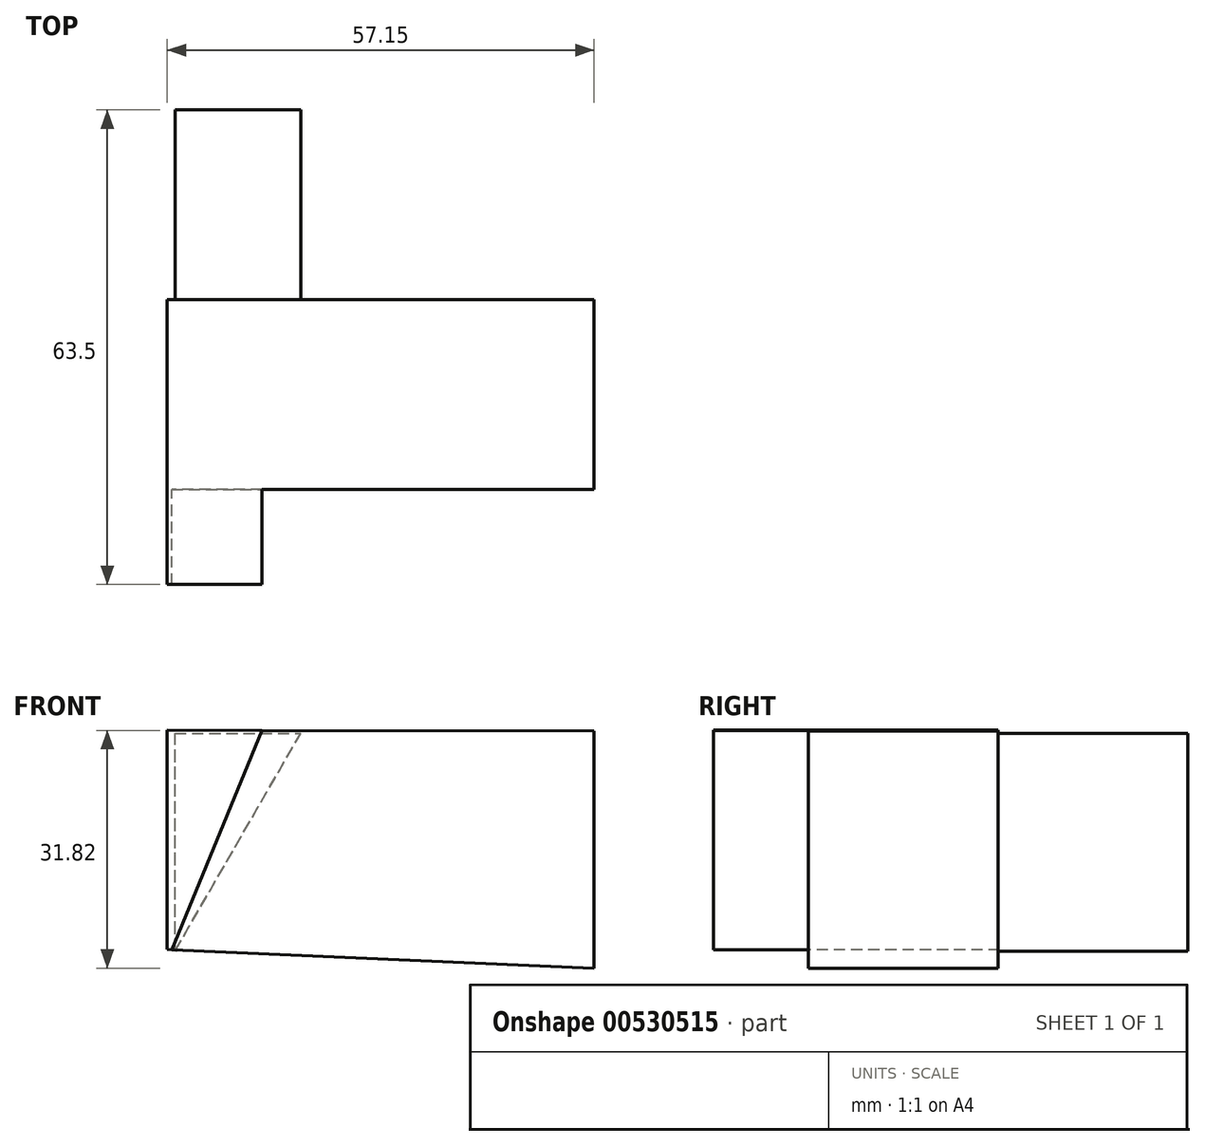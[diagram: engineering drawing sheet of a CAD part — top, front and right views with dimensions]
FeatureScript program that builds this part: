
annotation { "Feature Type Name" : "Feature", "Feature Type Description" : "" }
export const myFeature = defineFeature(function(context is Context, id is Id, definition is map)
    precondition{}
    {
        {
            var Q0;
            Q0=makeQuery(id+"FD3Ji2dYKjyLdMA_0.opExtrude","CAP_FACE",FACE,{"disambiguationData":[OSD([sQuery(id+"FqsT9jO7adyWTyq_0.wireOp",EDGE,"Xv4BoJzN-Ed49-FRgB-tAfS-qI5ulcrlhC3v"),sQuery(id+"FqsT9jO7adyWTyq_0.wireOp",EDGE,"Rq2qgrAZ-CMcJ-hNfP-7aXm-7j5Vf8qbodJT"),sQuery(id+"FqsT9jO7adyWTyq_0.wireOp",EDGE,"Tq6V1iMk-VQIz-2OuW-ugdr-rw9odok06HOZ"),sQuery(id+"FqsT9jO7adyWTyq_0.wireOp",EDGE,"m2H92b3s-GMAf-dQXL-fvXA-p3ciaarQUnOw")])],"isStart":false});
            var sketch = newSketch(context, id + "F0", { "sketchPlane" : qUnion([Q0])});
            skLineSegment(sketch, "E0", {"start": v(-10.45, 0) * mm, "end": v(-23.15, 31.75) * mm});
            skSolve(sketch);
        }
        {
            var Q0;
            Q0=qCreatedBy(makeId("Front.planeOp"),FACE);
            var sketch = newSketch(context, id + "F1", { "sketchPlane" : qUnion([Q0])});
            skLineSegment(sketch, "E1", {"start": v(-51.96, 14.93) * mm, "end": v(-51.96, -14.4) * mm});
            skLineSegment(sketch, "E2", {"start": v(-51.96, -14.4) * mm, "end": v(5.2, -16.9) * mm});
            skLineSegment(sketch, "E3", {"start": v(5.2, -16.9) * mm, "end": v(5.2, 14.86) * mm});
            skLineSegment(sketch, "E4", {"start": v(5.2, 14.86) * mm, "end": v(-51.96, 14.93) * mm});
            skSolve(sketch);
        }
        {
            var Q0;
            Q0 = qSketchRegion(id + "F1", true);
            extrude(context, id + "F2", {"entities" : qUnion([Q0]), "depth" : 25.4 * mm, "offsetDistance" : 25.4 * mm});
        }
        {
            var Q0;
            Q0=makeQuery(id+"F2.opExtrude","CAP_FACE",FACE,{"disambiguationData":[OSD([sQuery(id+"F1.wireOp",EDGE,"E1"),sQuery(id+"F1.wireOp",EDGE,"E2"),sQuery(id+"F1.wireOp",EDGE,"E3"),sQuery(id+"F1.wireOp",EDGE,"E4")])],"isStart":false});
            var sketch = newSketch(context, id + "F3", { "sketchPlane" : qUnion([Q0])});
            skLineSegment(sketch, "E5", {"start": v(-39.26, 14.92) * mm, "end": v(-51.37, -14.43) * mm});
            skLineSegment(sketch, "E6", {"start": v(-51.96, 14.93) * mm, "end": v(-39.26, 14.92) * mm});
            skLineSegment(sketch, "E7", {"start": v(-51.96, 14.93) * mm, "end": v(-51.96, -14.4) * mm});
            skLineSegment(sketch, "E8", {"start": v(-51.96, -14.4) * mm, "end": v(-51.37, -14.43) * mm});
            skSolve(sketch);
        }
        {
            var Q0;
            Q0=makeQuery(id+"F3.imprint","IMPRINT",FACE,{"disambiguationData":[TD([[makeQuery(id+"F3.imprint","IMPRINT",EDGE,{"derivedFrom":sQuery(id+"F3.wireOp",EDGE,"E5")}),-1.0]])]});
            var Q1;
            Q1=makeQuery(id+"F2.opExtrude","CAP_FACE",FACE,{"disambiguationData":[OSD([sQuery(id+"F1.wireOp",EDGE,"E1"),sQuery(id+"F1.wireOp",EDGE,"E2"),sQuery(id+"F1.wireOp",EDGE,"E3"),sQuery(id+"F1.wireOp",EDGE,"E4")])],"isStart":true});
            extrude(context, id + "F4", {"entities" : qUnion([Q0, Q1]), "operationType" : NewBodyOperationType.ADD, "depth" : 12.7 * mm, "offsetDistance" : 25.4 * mm});
        }
        {
            var Q0;
            Q0=makeQuery(id+"F2.opExtrude","CAP_FACE",FACE,{"disambiguationData":[OSD([sQuery(id+"F1.wireOp",EDGE,"E1"),sQuery(id+"F1.wireOp",EDGE,"E2"),sQuery(id+"F1.wireOp",EDGE,"E3"),sQuery(id+"F1.wireOp",EDGE,"E4")])],"isStart":true});
            var sketch = newSketch(context, id + "F5", { "sketchPlane" : qUnion([Q0])});
            skLineSegment(sketch, "E9", {"start": v(8.72, 14.88) * mm, "end": v(-3.06, -16.8) * mm});
            skSolve(sketch);
        }
        {
            var Q0;
            {var subQ0=sQuery(id+"F5.wireOp",EDGE,"E9");Q0=makeQuery(id+"F5.imprint","IMPRINT",FACE,{"disambiguationData":[TD([[makeQuery(id+"F5.imprint","IMPRINT",EDGE,{"derivedFrom":subQ0}),1.0]])]});}
            var sketch = newSketch(context, id + "F6", { "sketchPlane" : qUnion([Q0])});
            skLineSegment(sketch, "E10", {"start": v(50.93, -14.63) * mm, "end": v(34.08, 14.53) * mm});
            skLineSegment(sketch, "E11", {"start": v(50.93, -14.63) * mm, "end": v(50.93, 14.53) * mm});
            skLineSegment(sketch, "E12", {"start": v(50.93, 14.53) * mm, "end": v(34.08, 14.53) * mm});
            skSolve(sketch);
        }
        {
            var Q0;
            Q0 = qSketchRegion(id + "F6", true);
            extrude(context, id + "F7", {"entities" : qUnion([Q0]), "operationType" : NewBodyOperationType.ADD, "depth" : 25.4 * mm, "offsetDistance" : 25.4 * mm});
        }
    });
